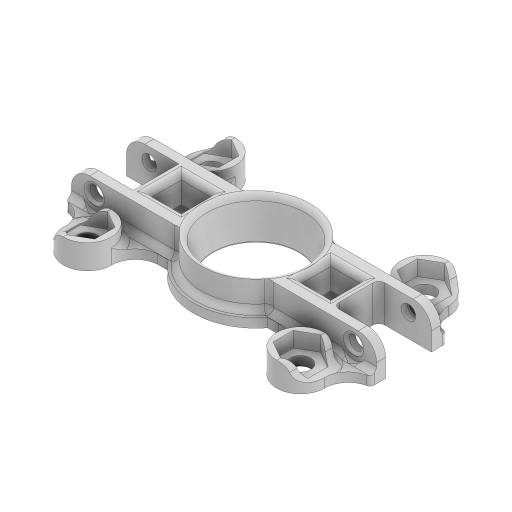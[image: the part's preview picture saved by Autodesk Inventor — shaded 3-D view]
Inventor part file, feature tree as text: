
AUTODESK INVENTOR PART (.ipt)
format: ipt  version: 2023 (Build 270158000, 158)  size: 1,361,408 bytes
history: native  units: in
note: dims shown in document units (in); Inventor stores cm internally (conversion verified against a paired STEP export)
features: sketch x11, extrude x10, fillet x8, projected_geometry x6, mirror x3, revolve x1
ambient origin geometry x8: Origin, YZ Plane, XZ Plane, XY Plane, X Axis, Y Axis, Z Axis, Center Point
bodies: Solid1 (feature_tree)
feature tree (39):
  extrude  "Extrusion1"  Depth=1.5748in
  extrude  "Extrusion2"  Depth=0.4134in
  fillet  "Fillet1"  Radius=1.517in
  extrude  "Extrusion3"  Depth=0.1181in
  fillet  "Fillet2"  Radius=0.4724in
  extrude  "Extrusion4"  Depth=0.3937in
  mirror  "Mirror1"
  fillet  "Fillet3"  Radius=0.5906in
  fillet  "Fillet4"  Radius=0.3937in
  revolve  "Revolution1"  [1 undecoded]
  fillet  "Fillet5"  Radius=0.185in
  extrude  "Extrusion5"  TaperAngle=0.0deg  [1 undecoded]
  extrude  "Extrusion7"  Depth=0.0394in
  extrude  "Extrusion8"  TaperAngle=90.0deg  [1 undecoded]
  extrude  "Extrusion9"  Depth=0.3937in
  fillet  "Fillet6"  Radius=0.3937in
  extrude  "Extrusion10"  Depth=0.1181in TaperAngle=0.0deg
  mirror  "Mirror2"
  extrude  "Extrusion11"  Depth=0.0591in
  mirror  "Mirror4"
  fillet  "Fillet7"  Radius=0.26in
  fillet  "Fillet8"  Radius=0.6157in
  sketch  "Sketch1"  dims[d0=3.937in d1=1.5748in]
  sketch  "Sketch2"  dims[d2=0.0787in d3=0.0in d6=0.4134in d8=1.517in]
  sketch  "Sketch3"  dims[d9=0.1181in d10=0.1181in d11=0.4724in d12=0.0in]
  sketch  "Sketch4"  dims[d13=0.0787in d14=1.1024in d16=0.5906in d17=0.3937in d18=0.0in]
  sketch  "Sketch5"  dims[d19=0.0787in d20=0.2953in d21=0.185in]
  projected_geometry  "Projected Loop1"
  sketch  "Sketch7"  dims[d22=0.2953in d23=0.0in d24=0.0in]
  sketch  "Sketch9"  dims[d25=0.2362in d26=0.0394in]
  projected_geometry  "Projected Loop2"
  sketch  "Sketch10"  dims[d27=0.0591in d28=90.0deg]
  projected_geometry  "Projected Loop3"
  projected_geometry  "Projected Loop4"
  projected_geometry  "Projected Loop5"
  projected_geometry  "Projected Loop8"
  sketch  "Sketch15"  dims[d29=0.0787in d30=3.937in d31=0.3937in d32=0.0in]
  sketch  "Sketch16"  dims[d37=0.0787in d38=0.0in d42=0.1181in d43=0.0in]
  sketch  "Sketch17"  dims[d62=2.75in d63=1.6in d64=0.26in d65=0.6157in d67=0.7874in d69=2.75in d70=0.3937in d72=0.3937in d74=0.0748in d75=1.6in d76=2.75in d77=0.2598in d78=0.7874in d80=1.6in d81=0.7874in d83=2.75in d86=0.1969in d87=0.0in d88=0.3543in d89=0.0in d90=0.0in d94=0.3543in d95=0.0in d96=0.0in d97=0.1417in d98=0.0591in d39=0.0197in d40=0.0344in d41=0.0197in]
note: 3 required parameter values undecoded (feature->parameter linkage not recoverable at this tier; creation-order binding heuristic only, values carry confidence <= 0.55)